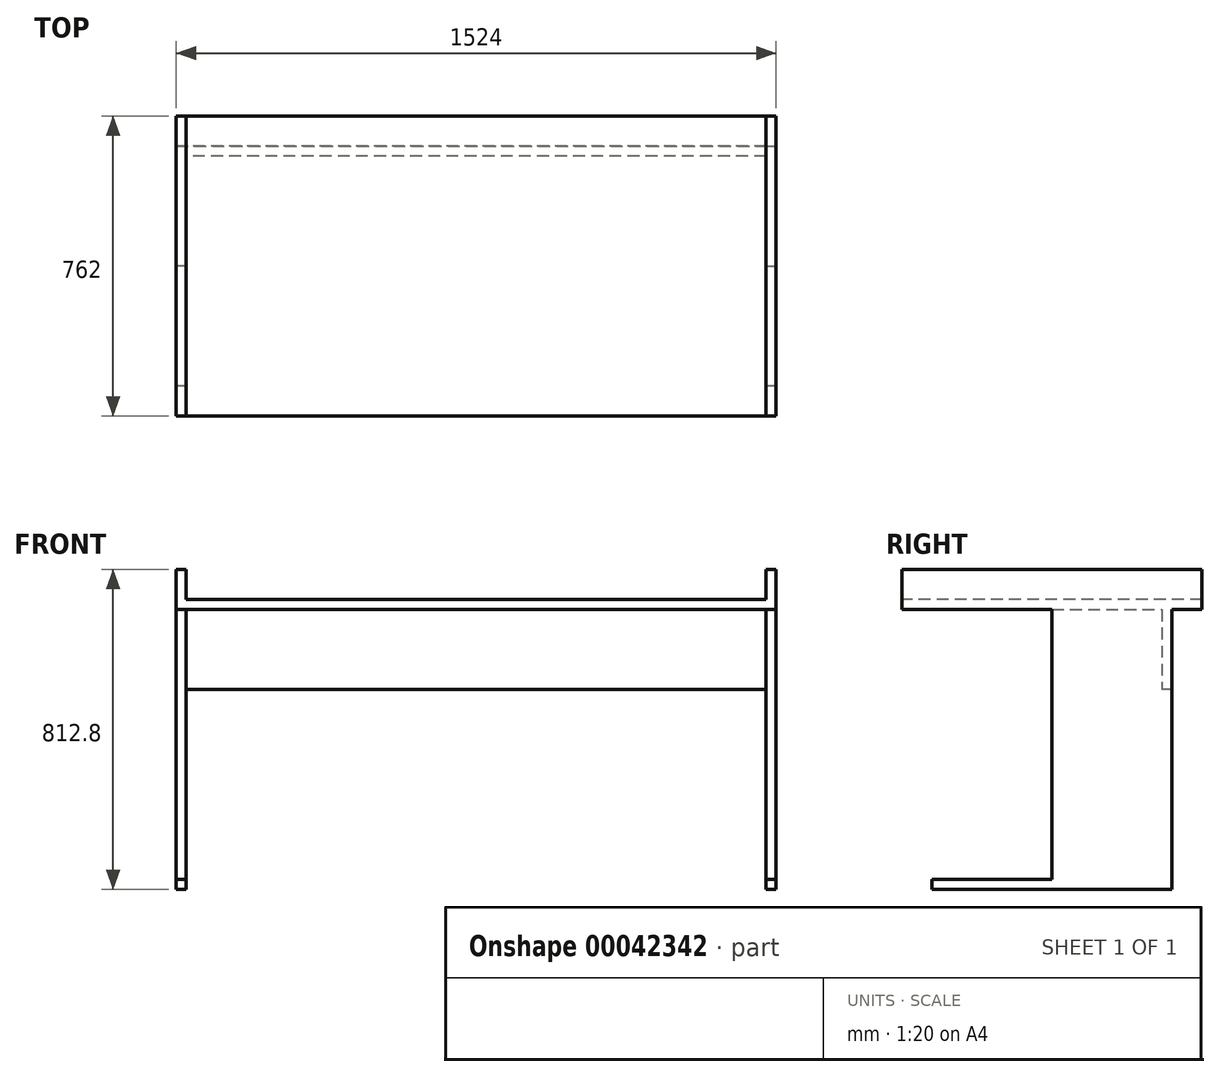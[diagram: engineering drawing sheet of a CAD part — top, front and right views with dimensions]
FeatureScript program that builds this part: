
annotation { "Feature Type Name" : "Feature", "Feature Type Description" : "" }
export const myFeature = defineFeature(function(context is Context, id is Id, definition is map)
    precondition{}
    {
        {
            var Q0;
            Q0=qCreatedBy(makeId("Top.planeOp"),FACE);
            var sketch = newSketch(context, id + "F0", { "sketchPlane" : qUnion([Q0])});
            skLineSegment(sketch, "E0.rect.bottom", {"start": v(762, 381) * mm, "end": v(-762, 381) * mm});
            skLineSegment(sketch, "E0.rect.top", {"start": v(762, -381) * mm, "end": v(-762, -381) * mm});
            skLineSegment(sketch, "E0.rect.left", {"start": v(762, 381) * mm, "end": v(762, -381) * mm});
            skLineSegment(sketch, "E0.rect.right", {"start": v(-762, 381) * mm, "end": v(-762, -381) * mm});
            skPoint(sketch, "E0.rect.middle", {"position": v(0, 0) * mm});
            skSolve(sketch);
        }
        {
            var Q0;
            Q0=makeQuery(id+"F0.imprint","IMPRINT",FACE,{"disambiguationData":[TD([[makeQuery(id+"F0.imprint","IMPRINT",EDGE,{"derivedFrom":sQuery(id+"F0.wireOp",EDGE,"E0.rect.bottom")}),1.0]])]});
            extrude(context, id + "F1", {"entities" : qUnion([Q0]), "oppositeDirection" : true, "depth" : 25.4 * mm});
        }
        {
            var Q0;
            Q0=makeQuery(id+"F1.opExtrude","CAP_FACE",FACE,{"disambiguationData":[OSD([sQuery(id+"F0.wireOp",EDGE,"E0.rect.bottom"),sQuery(id+"F0.wireOp",EDGE,"E0.rect.top"),sQuery(id+"F0.wireOp",EDGE,"E0.rect.left"),sQuery(id+"F0.wireOp",EDGE,"E0.rect.right")])],"isStart":false});
            var sketch = newSketch(context, id + "F2", { "sketchPlane" : qUnion([Q0])});
            skLineSegment(sketch, "E1.bottom", {"start": v(736.6, 0) * mm, "end": v(762, 0) * mm});
            skLineSegment(sketch, "E1.top", {"start": v(736.6, -304.8) * mm, "end": v(762, -304.8) * mm});
            skLineSegment(sketch, "E1.left", {"start": v(736.6, 0) * mm, "end": v(736.6, -304.8) * mm});
            skLineSegment(sketch, "E1.right", {"start": v(762, 0) * mm, "end": v(762, -304.8) * mm});
            skLineSegment(sketch, "E2.MirrorCS", {"start": v(-736.6, -304.8) * mm, "end": v(-762, -304.8) * mm});
            skLineSegment(sketch, "E3.MirrorCS", {"start": v(-736.6, 0) * mm, "end": v(-762, 0) * mm});
            skLineSegment(sketch, "E4.MirrorCS", {"start": v(-736.6, 0) * mm, "end": v(-736.6, -304.8) * mm});
            skLineSegment(sketch, "E5.MirrorCS", {"start": v(-762, 0) * mm, "end": v(-762, -304.8) * mm});
            skSolve(sketch);
        }
        {
            var Q0;
            Q0=qSketchRegion(id+"F2",true);
            extrude(context, id + "F3", {"entities" : qUnion([Q0]), "operationType" : NewBodyOperationType.ADD, "depth" : 685.8 * mm});
        }
        {
            var Q0;
            Q0=makeQuery(id+"F3.opExtrude","CAP_FACE",FACE,{"disambiguationData":[OSD([sQuery(id+"F2.wireOp",EDGE,"E1.bottom"),sQuery(id+"F2.wireOp",EDGE,"E1.top"),sQuery(id+"F2.wireOp",EDGE,"E1.left"),sQuery(id+"F2.wireOp",EDGE,"E1.right")])],"isStart":false});
            var sketch = newSketch(context, id + "F4", { "sketchPlane" : qUnion([Q0])});
            skLineSegment(sketch, "E6.bottom", {"start": v(762, -304.8) * mm, "end": v(736.6, -304.8) * mm});
            skLineSegment(sketch, "E6.top", {"start": v(762, 304.8) * mm, "end": v(736.6, 304.8) * mm});
            skLineSegment(sketch, "E6.left", {"start": v(762, -304.8) * mm, "end": v(762, 304.8) * mm});
            skLineSegment(sketch, "E6.right", {"start": v(736.6, -304.8) * mm, "end": v(736.6, 304.8) * mm});
            skSolve(sketch);
        }
        {
            var Q0;
            Q0=makeQuery(id+"F3.opExtrude","CAP_FACE",FACE,{"disambiguationData":[OSD([sQuery(id+"F2.wireOp",EDGE,"E2.MirrorCS"),sQuery(id+"F2.wireOp",EDGE,"E3.MirrorCS"),sQuery(id+"F2.wireOp",EDGE,"E4.MirrorCS"),sQuery(id+"F2.wireOp",EDGE,"E5.MirrorCS")])],"isStart":false});
            var sketch = newSketch(context, id + "F5", { "sketchPlane" : qUnion([Q0])});
            skLineSegment(sketch, "E7.bottom", {"start": v(-736.6, -304.8) * mm, "end": v(-762, -304.8) * mm});
            skLineSegment(sketch, "E7.top", {"start": v(-736.6, 304.8) * mm, "end": v(-762, 304.8) * mm});
            skLineSegment(sketch, "E7.left", {"start": v(-736.6, -304.8) * mm, "end": v(-736.6, 304.8) * mm});
            skLineSegment(sketch, "E7.right", {"start": v(-762, -304.8) * mm, "end": v(-762, 304.8) * mm});
            skSolve(sketch);
        }
        {
            var Q0;
            Q0=qSketchRegion(id+"F5",true);
            var Q1;
            Q1=qSketchRegion(id+"F4",true);
            extrude(context, id + "F6", {"entities" : qUnion([Q0, Q1]), "operationType" : NewBodyOperationType.ADD, "depth" : 25.4 * mm});
        }
        {
            var Q0;
            Q0=makeQuery(id+"F6.boolean.opBoolean","MERGE",FACE,{"derivedFrom":[makeQuery(id+"F3.opExtrude","SWEPT_FACE",FACE,{"disambiguationData":[OSD([sQuery(id+"F2.wireOp",EDGE,"E4.MirrorCS")])]}),makeQuery(id+"F6.opExtrude","SWEPT_FACE",FACE,{"disambiguationData":[OSD([sQuery(id+"F5.wireOp",EDGE,"E7.left")])]})]});
            var sketch = newSketch(context, id + "F7", { "sketchPlane" : qUnion([Q0])});
            skLineSegment(sketch, "E8.bottom", {"start": v(304.8, -25.4) * mm, "end": v(279.4, -25.4) * mm});
            skLineSegment(sketch, "E8.top", {"start": v(304.8, -228.6) * mm, "end": v(279.4, -228.6) * mm});
            skLineSegment(sketch, "E8.left", {"start": v(304.8, -25.4) * mm, "end": v(304.8, -228.6) * mm});
            skLineSegment(sketch, "E8.right", {"start": v(279.4, -25.4) * mm, "end": v(279.4, -228.6) * mm});
            skSolve(sketch);
        }
        {
            var Q0;
            Q0=qSketchRegion(id+"F7",true);
            extrude(context, id + "F8", {"entities" : qUnion([Q0]), "operationType" : NewBodyOperationType.ADD, "endBound" : BoundingType.UP_TO_NEXT, "depth" : 25.4 * mm});
        }
        {
            var Q0;
            Q0=makeQuery(id+"F1.opExtrude","CAP_FACE",FACE,{"disambiguationData":[OSD([sQuery(id+"F0.wireOp",EDGE,"E0.rect.bottom"),sQuery(id+"F0.wireOp",EDGE,"E0.rect.top"),sQuery(id+"F0.wireOp",EDGE,"E0.rect.left"),sQuery(id+"F0.wireOp",EDGE,"E0.rect.right")])],"isStart":true});
            var sketch = newSketch(context, id + "F9", { "sketchPlane" : qUnion([Q0])});
            skLineSegment(sketch, "E9.bottom", {"start": v(762, 381) * mm, "end": v(736.6, 381) * mm});
            skLineSegment(sketch, "E9.top", {"start": v(762, -381) * mm, "end": v(736.6, -381) * mm});
            skLineSegment(sketch, "E9.left", {"start": v(762, 381) * mm, "end": v(762, -381) * mm});
            skLineSegment(sketch, "E9.right", {"start": v(736.6, 381) * mm, "end": v(736.6, -381) * mm});
            skLineSegment(sketch, "E10.MirrorCS", {"start": v(-762, 381) * mm, "end": v(-736.6, 381) * mm});
            skLineSegment(sketch, "E11.MirrorCS", {"start": v(-762, -381) * mm, "end": v(-736.6, -381) * mm});
            skLineSegment(sketch, "E12.MirrorCS", {"start": v(-736.6, 381) * mm, "end": v(-736.6, -381) * mm});
            skLineSegment(sketch, "E13.MirrorCS", {"start": v(-762, 381) * mm, "end": v(-762, -381) * mm});
            skSolve(sketch);
        }
        {
            var Q0;
            Q0=qSketchRegion(id+"F9",true);
            extrude(context, id + "F10", {"entities" : qUnion([Q0]), "operationType" : NewBodyOperationType.ADD, "depth" : 76.2 * mm});
        }
    });
